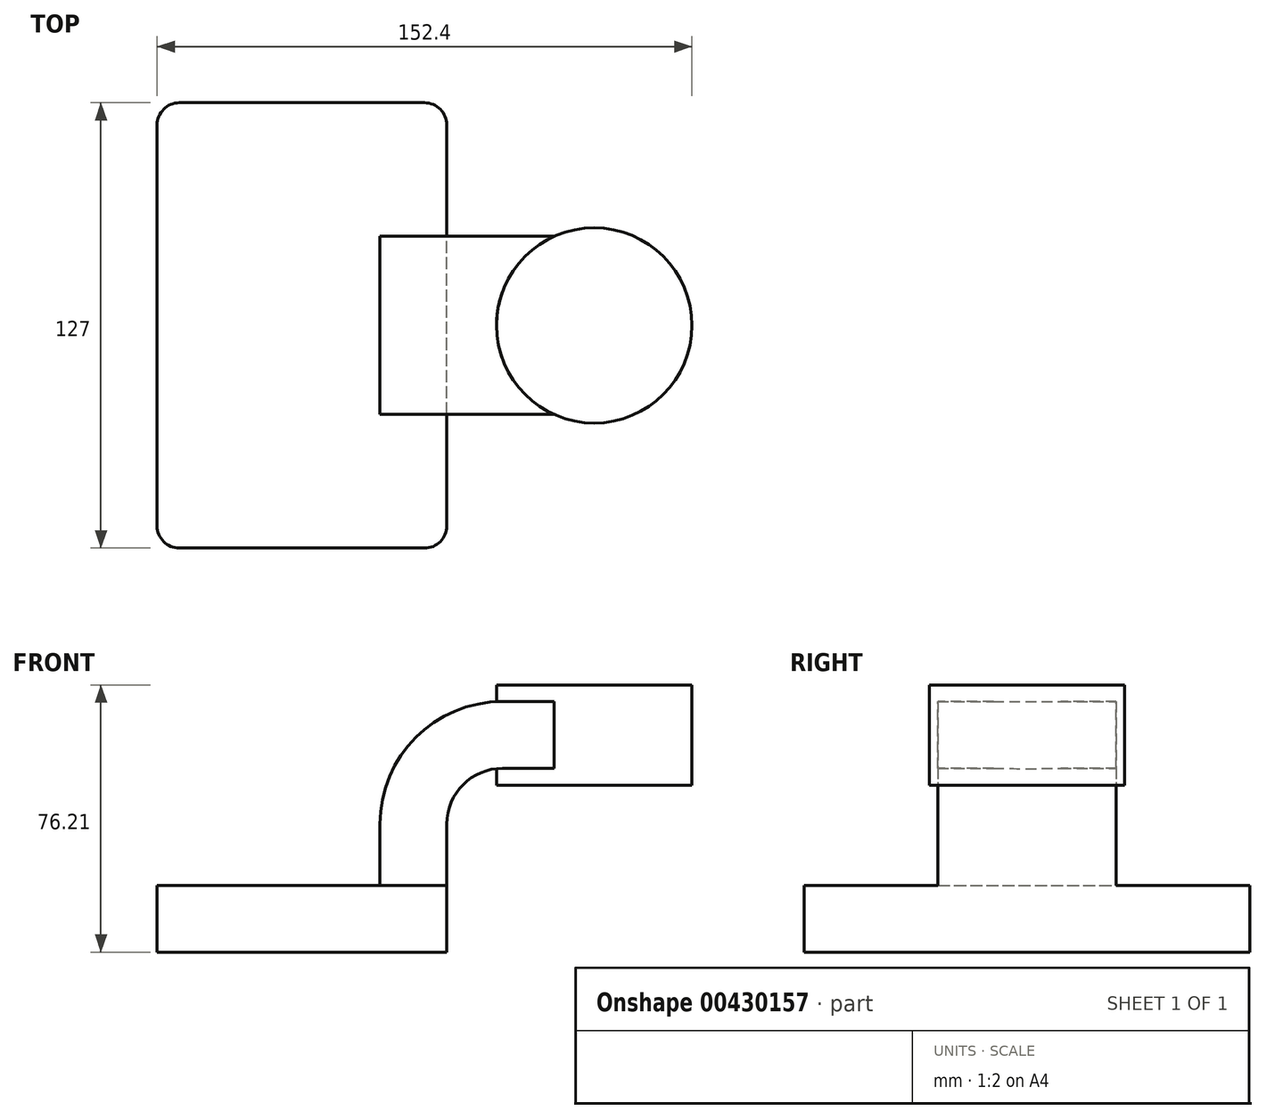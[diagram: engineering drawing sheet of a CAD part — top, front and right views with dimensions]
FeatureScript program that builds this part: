
annotation { "Feature Type Name" : "Feature", "Feature Type Description" : "" }
export const myFeature = defineFeature(function(context is Context, id is Id, definition is map)
    precondition{}
    {
        {
            var Q0;
            Q0=qCreatedBy(makeId("Front.planeOp"),FACE);
            var sketch = newSketch(context, id + "F0", { "sketchPlane" : qUnion([Q0])});
            skLineSegment(sketch, "E0.bottom", {"start": v(41.28, -9.52) * mm, "end": v(-41.28, -9.53) * mm});
            skLineSegment(sketch, "E0.top", {"start": v(41.28, 9.53) * mm, "end": v(-41.28, 9.53) * mm});
            skLineSegment(sketch, "E0.left", {"start": v(41.28, -9.52) * mm, "end": v(41.28, 9.53) * mm});
            skLineSegment(sketch, "E0.right", {"start": v(-41.28, -9.52) * mm, "end": v(-41.28, 9.53) * mm});
            skPoint(sketch, "E0.middle", {"position": v(0, 0) * mm});
            skLineSegment(sketch, "E1", {"start": v(41.28, 9.53) * mm, "end": v(41.28, 27) * mm});
            skLineSegment(sketch, "E2.bottom", {"start": v(60.32, 66.68) * mm, "end": v(111.12, 66.68) * mm});
            skLineSegment(sketch, "E2.top", {"start": v(60.32, 38.1) * mm, "end": v(111.12, 38.1) * mm});
            skLineSegment(sketch, "E2.left", {"start": v(60.32, 66.68) * mm, "end": v(60.32, 38.1) * mm});
            skLineSegment(sketch, "E2.right", {"start": v(111.12, 66.68) * mm, "end": v(111.12, 38.1) * mm});
            skPoint(sketch, "E2.middle", {"position": v(85.72, 52.39) * mm});
            skArc(sketch, "E3", {"start": v(41.27, 27) * mm, "mid": v(45.92, 38.23) * mm, "end": v(57.15, 42.88) * mm});
            skLineSegment(sketch, "E4", {"start": v(57.15, 42.88) * mm, "end": v(83.28, 42.88) * mm});
            skLineSegment(sketch, "E5.0", {"start": v(57.15, 61.93) * mm, "end": v(83.28, 61.93) * mm});
            skArc(sketch, "E5.1", {"start": v(22.23, 27) * mm, "mid": v(32.45, 51.7) * mm, "end": v(57.15, 61.93) * mm});
            skLineSegment(sketch, "E5.2", {"start": v(22.22, 9.53) * mm, "end": v(22.22, 27) * mm});
            skLineSegment(sketch, "E6", {"start": v(83.28, 66.68) * mm, "end": v(83.28, 38.1) * mm});
            skFitSpline(sketch, "E7", {"points": [v(-41.28, 9.53) * mm, v(57.15, 61.93) * mm], "startDerivative": vector(1.16, 83.8) * mm, "endDerivative": vector(171.45, -2.84) * mm});
            skSolve(sketch);
        }
        {
            var Q0;
            Q0=makeQuery(id+"F0.imprint","IMPRINT",FACE,{"disambiguationData":[TD([[makeQuery(id+"F0.imprint","IMPRINT",EDGE,{"derivedFrom":sQuery(id+"F0.wireOp",EDGE,"E0.bottom")}),-1.0]])]});
            extrude(context, id + "F1", {"entities" : qUnion([Q0]), "endBound" : BoundingType.SYMMETRIC, "depth" : 127 * mm});
        }
        {
            var Q0;
            {var subQ1=sQuery(id+"F0.wireOp",EDGE,"E1");Q0=makeQuery(id+"F0.imprint","IMPRINT",FACE,{"disambiguationData":[TD([[makeQuery(id+"F0.imprint","IMPRINT",EDGE,{"derivedFrom":subQ1}),1.0]])]});}
            var Q1;
            {var subQ0=sQuery(id+"F0.wireOp",EDGE,"E5.0");var subQ1=sQuery(id+"F0.wireOp",EDGE,"E2.left");var subQ2=makeQuery(id+"F0.imprint","INTERSECT",VERTEX,{"derivedFrom":[subQ1,subQ0]});Q1=makeQuery(id+"F0.imprint","IMPRINT",FACE,{"disambiguationData":[TD([[makeQuery(id+"F0.imprint","IMPRINT",EDGE,{"disambiguationData":[TD([[subQ2,-1.0]])],"derivedFrom":subQ1}),1.0]])]});}
            extrude(context, id + "F2", {"entities" : qUnion([Q0, Q1]), "operationType" : NewBodyOperationType.ADD, "endBound" : BoundingType.SYMMETRIC, "depth" : 50.8 * mm});
        }
        {
            var Q0;
            Q0=makeQuery(id+"F0.imprint","IMPRINT",FACE,{"disambiguationData":[TD([[makeQuery(id+"F0.imprint","IMPRINT",EDGE,{"derivedFrom":sQuery(id+"F0.wireOp",EDGE,"E5.1")}),1.0]])]});
            extrude(context, id + "F3", {"entities" : qUnion([Q0]), "operationType" : NewBodyOperationType.ADD, "endBound" : BoundingType.SYMMETRIC, "depth" : 15.88 * mm});
        }
        {
            var Q0;
            {var subQ4=sQuery(id+"F0.wireOp",EDGE,"E2.right");Q0=makeQuery(id+"F0.imprint","IMPRINT",FACE,{"disambiguationData":[TD([[makeQuery(id+"F0.imprint","IMPRINT",EDGE,{"derivedFrom":subQ4}),-1.0]])]});}
            var Q1;
            Q1=sQuery(id+"F0.wireOp",EDGE,"E6");
            revolve(context, id + "F4", {"operationType" : NewBodyOperationType.ADD, "entities" : qUnion([Q0]), "axis" : qUnion([Q1]), "revolveType" : RevolveType.FULL});
        }
        {
            var Q0;
            Q0=makeQuery(id+"F1.opExtrude","CAP_EDGE",EDGE,{"disambiguationData":[OSD([sQuery(id+"F0.wireOp",EDGE,"E0.right")])],"isStart":false});
            var Q1;
            Q1=makeQuery(id+"F1.opExtrude","CAP_EDGE",EDGE,{"disambiguationData":[OSD([sQuery(id+"F0.wireOp",EDGE,"E0.left")])],"isStart":false});
            var Q2;
            Q2=makeQuery(id+"F1.opExtrude","CAP_EDGE",EDGE,{"disambiguationData":[OSD([sQuery(id+"F0.wireOp",EDGE,"E0.left")])],"isStart":true});
            var Q3;
            Q3=makeQuery(id+"F1.opExtrude","CAP_EDGE",EDGE,{"disambiguationData":[OSD([sQuery(id+"F0.wireOp",EDGE,"E0.right")])],"isStart":true});
            fillet(context, id + "F5", {"entities" : qUnion([Q0, Q1, Q2, Q3]), "radius" : 6.35 * mm, "tangentPropagation" : true, "allowEdgeOverflow" : false});
        }
    });
